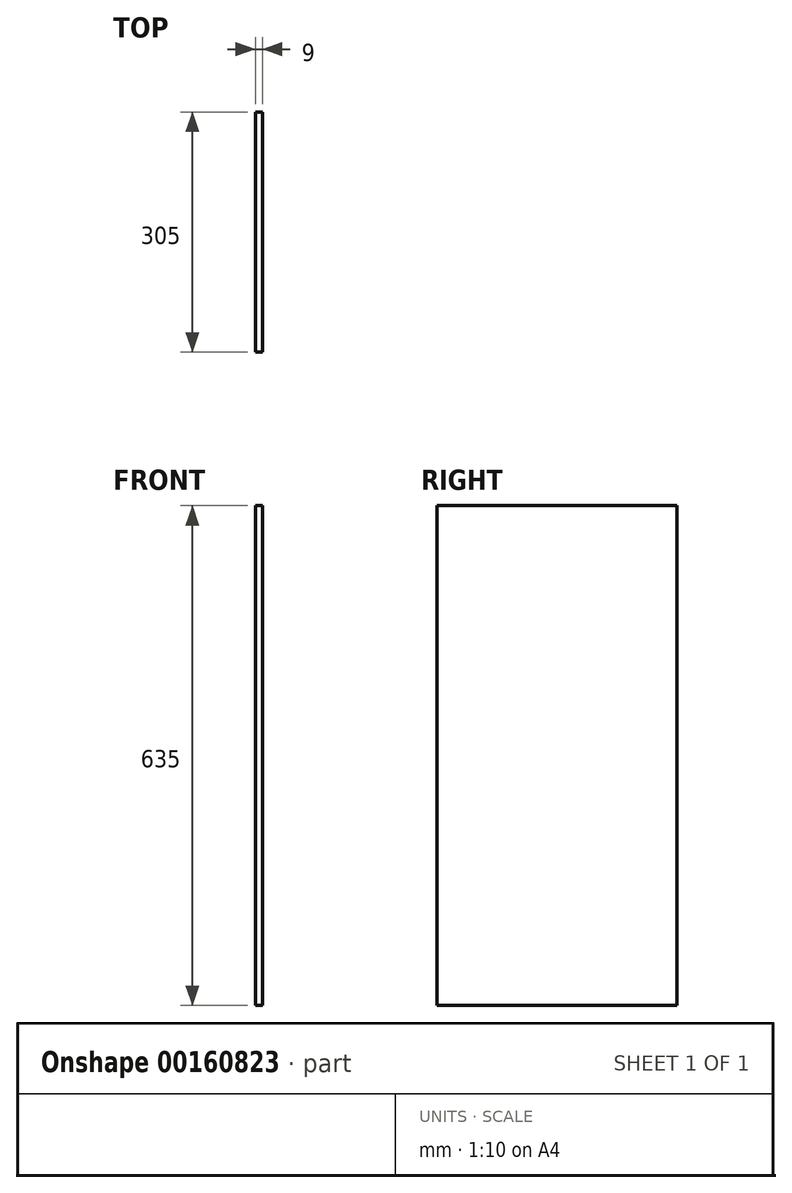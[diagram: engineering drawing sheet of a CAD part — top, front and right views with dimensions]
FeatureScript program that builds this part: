
annotation { "Feature Type Name" : "Feature", "Feature Type Description" : "" }
export const myFeature = defineFeature(function(context is Context, id is Id, definition is map)
    precondition{}
    {
        {
            var Q0;
            Q0=qCreatedBy(makeId("Right.planeOp"),FACE);
            var sketch = newSketch(context, id + "F0", { "sketchPlane" : qUnion([Q0])});
            skLineSegment(sketch, "E0.bottom", {"start": v(0, 0) * mm, "end": v(-305, 0) * mm});
            skLineSegment(sketch, "E0.top", {"start": v(0, 635) * mm, "end": v(-305, 635) * mm});
            skLineSegment(sketch, "E0.left", {"start": v(0, 0) * mm, "end": v(0, 635) * mm});
            skLineSegment(sketch, "E0.right", {"start": v(-305, 0) * mm, "end": v(-305, 635) * mm});
            skSolve(sketch);
        }
        {
            var Q0;
            Q0=qSketchRegion(id+"F0",true);
            extrude(context, id + "F1", {"entities" : qUnion([Q0]), "depth" : 9 * mm});
        }
    });
